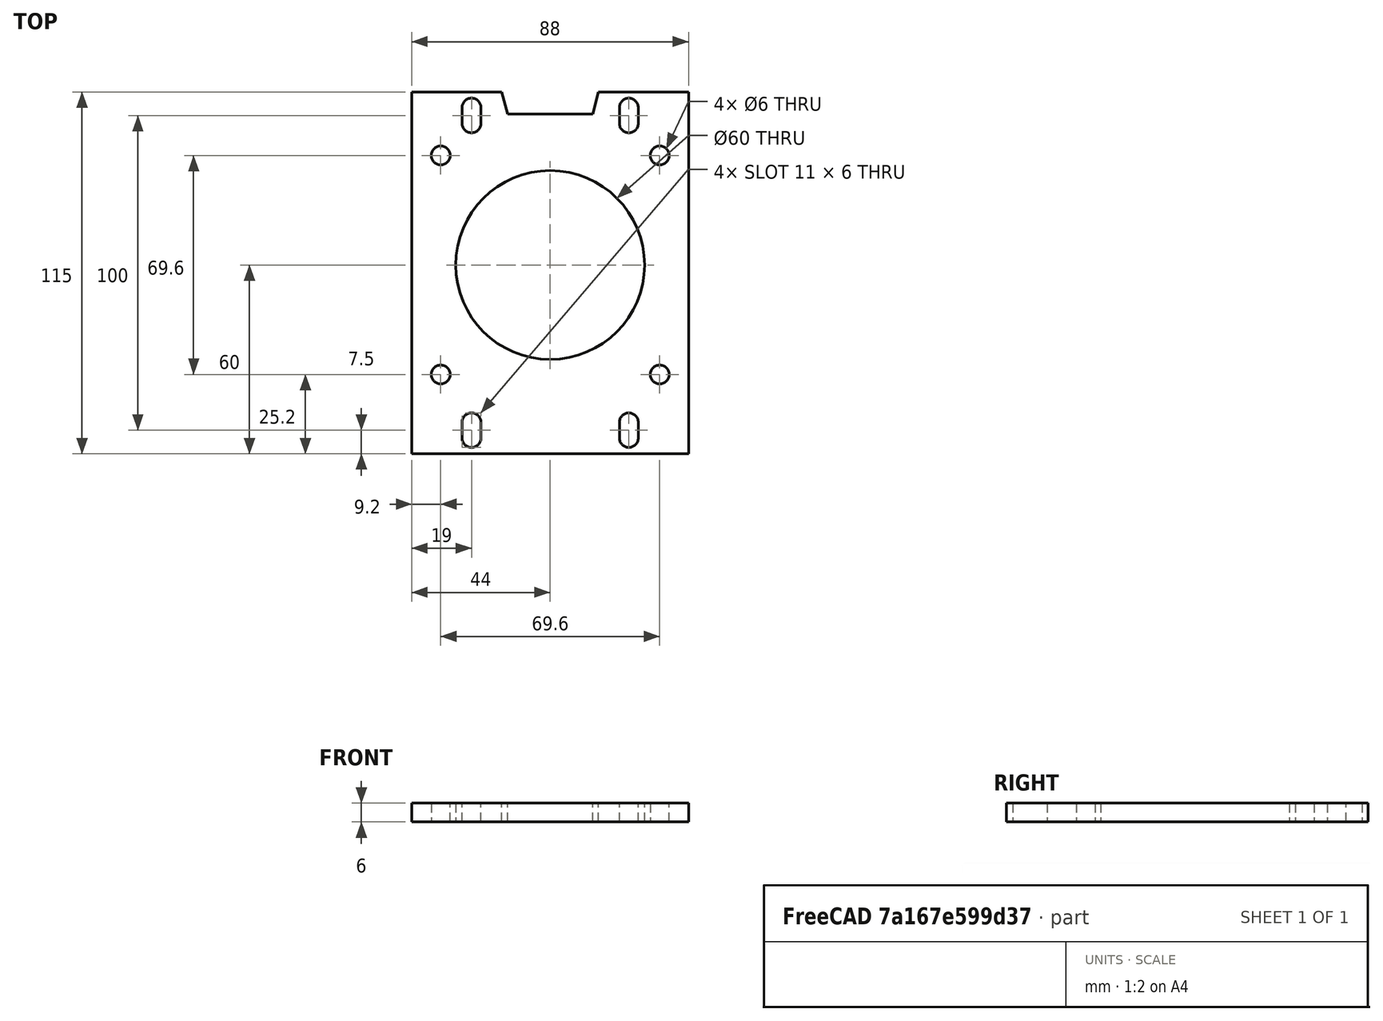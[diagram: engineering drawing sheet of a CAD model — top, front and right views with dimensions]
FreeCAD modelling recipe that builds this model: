
FCSTD DOCUMENT  (FreeCAD 0.16R5636 (Git))
Label: Motor-connect-plate-4
License: CreativeCommons Attribution-ShareAlike
LicenseURL: http://creativecommons.org/licenses/by-sa/4.0/
objects: Sketcher::SketchObject×1, PartDesign::Pad×1
note: 3 computed .brp shape members not serialized (recipe doc carries the construction recipe); baked Part::Feature solids carry a one-line shape summary decoded from their .brp

FEATURE [Sketcher::SketchObject] Sketch
  sketch-geometry (29):
    g0: LineSegment StartX=44 StartY=115 StartZ=0 EndX=44 EndY=0 EndZ=0
    g1: LineSegment StartX=44 StartY=0 StartZ=0 EndX=-44 EndY=0 EndZ=0
    g2: LineSegment StartX=-44 StartY=0 StartZ=0 EndX=-44 EndY=115 EndZ=0
    g3: Circle CenterX=0 CenterY=60 CenterZ=0 NormalX=0 NormalY=0 NormalZ=1 Radius=30
    g4: ArcOfCircle CenterX=-25 CenterY=110 CenterZ=0 NormalX=0 NormalY=0 NormalZ=1 Radius=3 StartAngle=0 EndAngle=3.14159
    g5: ArcOfCircle CenterX=-25 CenterY=105 CenterZ=0 NormalX=0 NormalY=0 NormalZ=1 Radius=3 StartAngle=3.14159 EndAngle=6.28319
    g6: LineSegment StartX=-28 StartY=110 StartZ=0 EndX=-28 EndY=105 EndZ=0
    g7: LineSegment StartX=-22 StartY=110 StartZ=0 EndX=-22 EndY=105 EndZ=0
    g8: ArcOfCircle CenterX=25 CenterY=110 CenterZ=0 NormalX=0 NormalY=0 NormalZ=1 Radius=3 StartAngle=0 EndAngle=3.14159
    g9: ArcOfCircle CenterX=25 CenterY=105 CenterZ=0 NormalX=0 NormalY=0 NormalZ=1 Radius=3 StartAngle=3.14159 EndAngle=6.28319
    g10: LineSegment StartX=22 StartY=110 StartZ=0 EndX=22 EndY=105 EndZ=0
    g11: LineSegment StartX=28 StartY=110 StartZ=0 EndX=28 EndY=105 EndZ=0
    g12: ArcOfCircle CenterX=25 CenterY=10 CenterZ=0 NormalX=0 NormalY=0 NormalZ=1 Radius=3 StartAngle=0 EndAngle=3.14159
    g13: ArcOfCircle CenterX=25 CenterY=5 CenterZ=0 NormalX=0 NormalY=0 NormalZ=1 Radius=3 StartAngle=3.14159 EndAngle=6.28319
    g14: LineSegment StartX=22 StartY=10 StartZ=0 EndX=22 EndY=5 EndZ=0
    g15: LineSegment StartX=28 StartY=10 StartZ=0 EndX=28 EndY=5 EndZ=0
    g16: ArcOfCircle CenterX=-25 CenterY=10 CenterZ=0 NormalX=0 NormalY=0 NormalZ=1 Radius=3 StartAngle=0 EndAngle=3.14159
    g17: ArcOfCircle CenterX=-25 CenterY=5 CenterZ=0 NormalX=0 NormalY=0 NormalZ=1 Radius=3 StartAngle=3.14159 EndAngle=6.28319
    g18: LineSegment StartX=-28 StartY=10 StartZ=0 EndX=-28 EndY=5 EndZ=0
    g19: LineSegment StartX=-22 StartY=10 StartZ=0 EndX=-22 EndY=5 EndZ=0
    g20: LineSegment StartX=-44 StartY=115 StartZ=0 EndX=-15.3756 EndY=115 EndZ=0
    g21: LineSegment StartX=-15.3756 StartY=115 StartZ=0 EndX=-13.5 EndY=108 EndZ=0
    g22: LineSegment StartX=-13.5 StartY=108 StartZ=0 EndX=13.5 EndY=108 EndZ=0
    g23: LineSegment StartX=13.5 StartY=108 StartZ=0 EndX=15.3756 EndY=115 EndZ=0
    g24: LineSegment StartX=15.3756 StartY=115 StartZ=0 EndX=44 EndY=115 EndZ=0
    g25: Circle CenterX=-34.8 CenterY=94.8 CenterZ=0 NormalX=0 NormalY=0 NormalZ=1 Radius=3
    g26: Circle CenterX=34.8 CenterY=94.8 CenterZ=0 NormalX=0 NormalY=0 NormalZ=1 Radius=3
    g27: Circle CenterX=-34.8 CenterY=25.2 CenterZ=0 NormalX=0 NormalY=0 NormalZ=1 Radius=3
    g28: Circle CenterX=34.8 CenterY=25.2 CenterZ=0 NormalX=0 NormalY=0 NormalZ=1 Radius=3
  constraints (74):
    c: Coincident(g0,g1)
    c: Coincident(g1,g2)
    c: Horizontal(g1)
    c: Vertical(g0)
    c: Vertical(g2)
    c: Symmetric(g2,g0,g-2)
    c: PointOnObject(g0,g-1)
    c: DistanceX(g1,g0) = 88
    c: DistanceY(g0,g0) = 115
    c: PointOnObject(g3,g-2)
    c: Tangent(g4,g7) = 1.5708
    c: Tangent(g4,g6) = -1.5708
    c: Tangent(g6,g5) = -1.5708
    c: Tangent(g7,g5) = 1.5708
    c: Vertical(g6)
    c: Equal(g4,g5)
    c: Tangent(g8,g11) = 1.5708
    c: Tangent(g8,g10) = -1.5708
    c: Tangent(g10,g9) = -1.5708
    c: Tangent(g11,g9) = 1.5708
    c: Vertical(g10)
    c: Equal(g8,g9)
    c: Tangent(g12,g15) = 1.5708
    c: Tangent(g12,g14) = -1.5708
    c: Tangent(g14,g13) = -1.5708
    c: Tangent(g15,g13) = 1.5708
    c: Vertical(g14)
    c: Equal(g12,g13)
    c: Tangent(g16,g19) = 1.5708
    c: Tangent(g16,g18) = -1.5708
    c: Tangent(g18,g17) = -1.5708
    c: Tangent(g19,g17) = 1.5708
    c: Vertical(g18)
    c: Equal(g16,g17)
    c: Symmetric(g5,g9,g-2)
    c: Symmetric(g16,g12,g-2)
    c: Equal(g4,g8)
    c: Equal(g8,g16)
    c: Equal(g16,g12)
    c: Equal(g7,g10)
    c: Equal(g10,g19)
    c: Equal(g19,g14)
    c: Radius(g8) = 3
    c: Radius(g3) = 30
    c: DistanceY(g8,g0) = 5
    c: DistanceY(g13,g0) = -5
    c: DistanceY(g5,g4) = 5
    c: DistanceX(g16,g12) = 50
    c: DistanceX(g5,g9) = 50
    c: DistanceY(g-1,g3) = 60
    c: Coincident(g20,g21)
    c: Coincident(g21,g22)
    c: Coincident(g22,g23)
    c: Coincident(g23,g24)
    c: Coincident(g0,g24)
    c: Coincident(g20,g2)
    c: Horizontal(g20)
    c: Horizontal(g22)
    c: Horizontal(g24)
    c: Symmetric(g20,g23,g-2)
    c: DistanceX(g21,g22) = 27
    c: Angle(g20,g21) = 1.8326
    c: Angle(g23,g24) = 1.8326
    c: DistanceY(g22,g23) = 7
    c: Symmetric(g28,g27,g-2)
    c: Symmetric(g25,g26,g-2)
    c: DistanceX(g27,g28) = 69.6
    c: Equal(g25,g27)
    c: Equal(g27,g28)
    c: Equal(g28,g26)
    c: Radius(g28) = 3
    c: DistanceY(g27,g25) = 69.6
    c: DistanceX(g25,g26) = 69.6
    c: DistanceY(g3,g25) = 34.8
FEATURE [PartDesign::Pad] Pad
  Length = 6
  Length2 = 100
  Sketch = -> Sketch
  Type = 0
